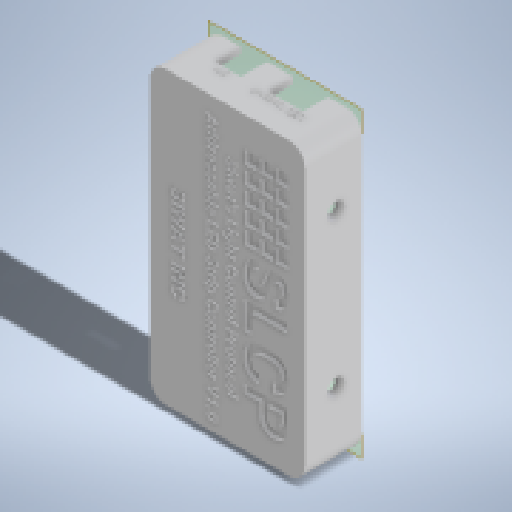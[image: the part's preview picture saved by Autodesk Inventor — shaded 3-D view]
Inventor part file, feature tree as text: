
AUTODESK INVENTOR PART (.ipt)
format: ipt  version: 2023 (Build 270158000, 158)  size: 2,656,768 bytes
history: native  units: in
note: dims shown in document units (in); Inventor stores cm internally (conversion verified against a paired STEP export)
features: reference x28, extrude x13, sketch x12, projected_geometry x4, other x3, plane x2, chamfer x1
ambient origin geometry x8: Origin, YZ Plane, XZ Plane, XY Plane, X Axis, Y Axis, Z Axis, Center Point
bodies: Solid1 (feature_tree)
feature tree (63):
  plane  "Work Plane1"
  extrude  "Extrusion1"  Depth=0.0591in
  extrude  "Extrusion2"  Depth=2.0438in TaperAngle=0.0deg
  extrude  "Extrusion3"  Depth=0.0079in
  extrude  "Extrusion4"  Depth=0.0079in TaperAngle=0.0deg
  sketch  "Sketch5"  dims[d13=0.0984in d14=0.0in d15=0.1644in d16=0.0in]
  plane  "Work Plane2"
  extrude  "Extrusion5"  Depth=0.1644in TaperAngle=0.0deg
  extrude  "Extrusion6"  Depth=0.248in TaperAngle=0.0deg
  extrude  "Extrusion7"  Depth=0.0118in
  extrude  "Extrusion8"  Depth=0.0118in
  chamfer  "Chamfer2"  Distance=0.248in
  extrude  "Extrusion9"  Depth=0.0079in
  extrude  "Extrusion10"  Depth=0.0098in TaperAngle=0.0deg
  extrude  "Extrusion11"  Depth=0.1181in
  extrude  "Extrusion12"  Depth=0.0079in
  extrude  "Extrusion13"  Depth=0.0079in TaperAngle=0.0deg
  sketch  "Sketch1"  dims[d0=0.0118in d1=0.0591in]
  reference  "Reference1"
  sketch  "Sketch2"  dims[d2=0.4188in d3=0.0in d4=2.0438in d5=2.0438in d6=0.0in d7=0.0in]
  reference  "Reference2"
  reference  "Reference3"
  sketch  "Sketch3"  dims[d8=0.0236in d9=0.0079in]
  reference  "Reference4"
  sketch  "Sketch4"  dims[d10=0.0079in d11=2.0438in d12=0.0in]
  reference  "Reference5"
  reference  "Reference6"
  reference  "Reference7"
  reference  "Reference8"
  reference  "Reference9"
  reference  "Reference10"
  reference  "Reference11"
  reference  "Reference12"
  reference  "Reference13"
  reference  "Reference14"
  reference  "Reference15"
  reference  "Reference16"
  reference  "Reference17"
  reference  "Reference18"
  reference  "Reference19"
  reference  "Reference20"
  reference  "Reference21"
  reference  "Reference22"
  reference  "Reference23"
  reference  "Reference24"
  reference  "Reference25"
  reference  "Reference26"
  reference  "Reference27"
  reference  "Reference28"
  sketch  "Sketch7"  dims[d17=0.1969in d18=0.0in d19=0.248in d20=0.0in]
  sketch  "Sketch8"  dims[d21=0.0118in d22=0.0118in]
  projected_geometry  "Projected Loop1"
  sketch  "Sketch9"  dims[d23=0.0118in d24=0.0118in d25=0.248in d26=0.0in]
  projected_geometry  "Projected Loop2"
  projected_geometry  "Projected Loop3"
  projected_geometry  "Projected Loop4"
  sketch  "Sketch10"  dims[d30=0.0079in d31=0.0079in]
  sketch  "Sketch11"  dims[d32=0.0315in d33=0.0787in d34=60.0deg d35=0.0098in d36=0.0in]
  sketch  "Sketch12"  dims[d37=0.1181in d38=0.1181in]
  sketch  "Sketch13"  dims[d39=0.0394in d40=1.9685in d42=0.1575in d43=1.1811in d45=0.1378in d48=0.0394in d49=0.0in d50=0.0079in d51=0.0in d52=0.0079in d53=0.0in d54=0.0079in d55=0.0in]
  parser-record x1  (decoder bookkeeping rows leaked as tree rows — omitted from the tree; the rows remain in map.json)
  other  "Casing.iam"
  other  "Base:1"
note: 1 file-system path scrubbed to <path> (originals preserved in map.json)
